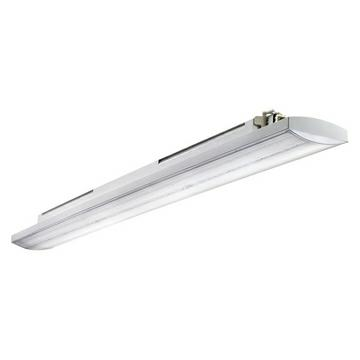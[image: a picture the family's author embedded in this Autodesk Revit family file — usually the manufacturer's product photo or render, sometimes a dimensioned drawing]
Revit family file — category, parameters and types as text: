
# Revit family: Lighting-Industrial-GEWISS-SMART[3]PLUS-WATERTIGHT-LED-EMERGENCY_TRANSPARENT_1200mm
name_source: partatom
category: Apparecchi per illuminazione
units: mm (PartAtom-declared; Revit-internal decimal feet)

## family parameters
Condiviso = No
Host = Superficie
Punto di calcolo locali = No
Quota connettore circolare = Usa diametro
Sorgente d'illuminazione = No
Taglio con vuoti quando caricato = No
Tipo di parte = Normale

## types (1)
- Lighting-Industrial-GEWISS-SMART[3]PLUS-WATERTIGHT-LED-EMERGENCY_TRANSPARENT_1200mm
    Application = Indoor
    Carico apparente = 56 VA
    Catalogue = LIGHTING
    Catalogue Range = SMART[3] PLUS
    Colour temperature = 5700 K (CRI > 90)
    Colour temperature: = 5700 K (CRI > 90)
    Commenti sul wattaggio = 56W
    Descrizione = SMART3 PLUS 1200 EMERG DT1+DT6 HE TRASP 9 57
    Efficiency class of integrated LEDs = A ÷ A++
    Electrocod = 2434
    Ganci = GEWISS  - ALLUMINIO
    Glow Wire Test = 850°C
    IDF = 9f0aacd4-2dae-44e9-b110-049f8c510713
    IDT = 4cee24bc-7d08-4ab8-ad84-39fd04b56e2f
    IP degree = IP66/IP69
    Immagine tipo = GWS3136T.jpg
    Insulation class = II
    Lamp = LED
    Lampada = LED
    Length = 1200 mm
    Lumen output (lm) = 4500
    Lunghezza Lampada = 1200 mm
    Modello = GWS3225AT957
    Operating temperature: = ND
    Produttore = GEWISS S.p.A.
    Prospetto di default = 1219 mm
    SEO = Ceiling
    Schermo. = Gewiss - Led Acceso
    Shield type = Transparent
    Shock resistance = IK08
    Stampa 1_100 = Sì
    Stampa 1_200 = No
    Struttura = GEWISS - SMART 3 - GRIGIO
    System power = 36 W
    Technical sheet = https://www.gewiss.com
    Type of light source = LED - Not replaceable
    URL = https://www.gewiss.com
    Version file RFA = 20.0
    Voltage = 220-240 V
    Warranty = ND
    Working temperature = ND
